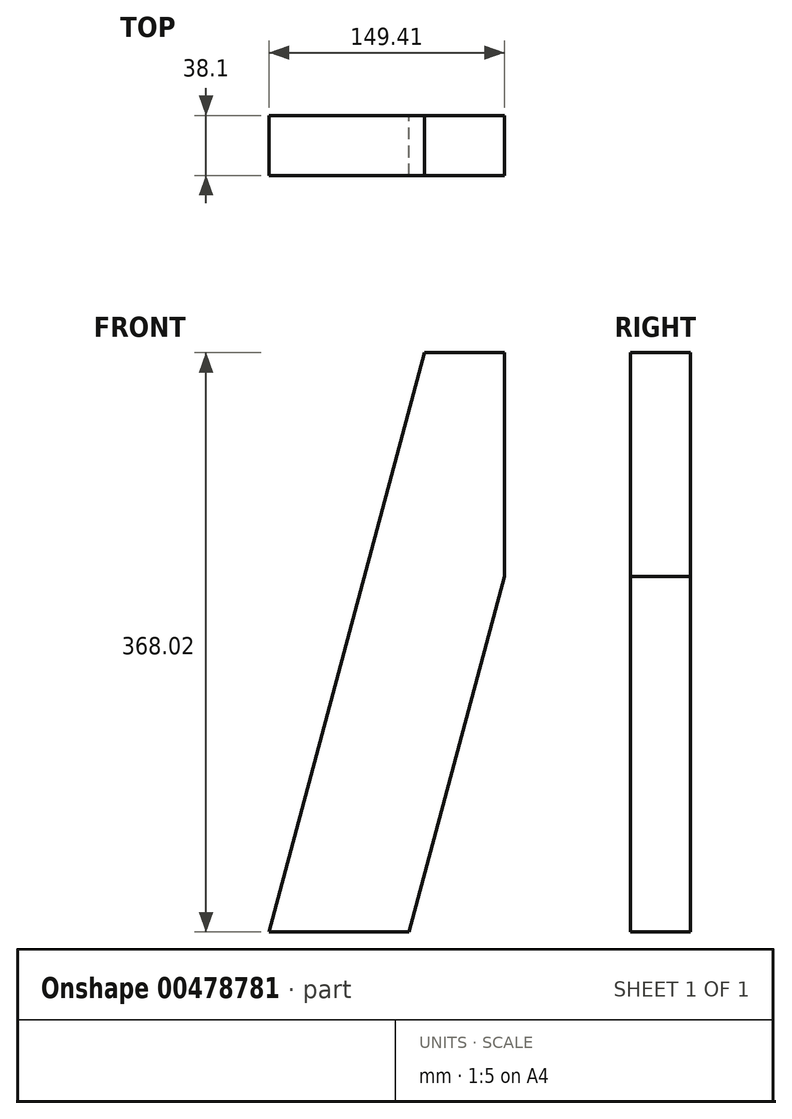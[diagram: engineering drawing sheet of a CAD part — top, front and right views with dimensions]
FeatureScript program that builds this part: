
annotation { "Feature Type Name" : "Feature", "Feature Type Description" : "" }
export const myFeature = defineFeature(function(context is Context, id is Id, definition is map)
    precondition{}
    {
        {
            var Q0;
            Q0=qCreatedBy(makeId("Front.planeOp"),FACE);
            var sketch = newSketch(context, id + "F0", { "sketchPlane" : qUnion([Q0])});
            skLineSegment(sketch, "E0", {"start": v(0, 0) * mm, "end": v(98.61, 368.02) * mm});
            skLineSegment(sketch, "E1", {"start": v(98.61, 368.02) * mm, "end": v(149.41, 368.02) * mm});
            skLineSegment(sketch, "E2", {"start": v(149.41, 368.02) * mm, "end": v(149.41, 225.83) * mm});
            skLineSegment(sketch, "E3", {"start": v(149.41, 225.83) * mm, "end": v(88.9, 0) * mm});
            skLineSegment(sketch, "E4", {"start": v(88.9, 0) * mm, "end": v(0, 0) * mm});
            skSolve(sketch);
        }
        {
            var Q0;
            Q0 = qSketchRegion(id + "F0", true);
            extrude(context, id + "F1", {"entities" : qUnion([Q0]), "depth" : 38.1 * mm});
        }
    });
